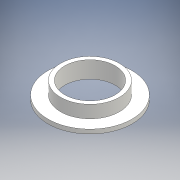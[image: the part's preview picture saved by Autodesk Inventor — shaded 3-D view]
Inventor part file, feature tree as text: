
AUTODESK INVENTOR PART (.ipt)
format: ipt  version: 2016 (Build 200138000, 138)  size: 103,936 bytes
history: native  units: mm
features: extrude x2, other x1, sketch x1
ambient origin geometry x8: Origin, YZ Plane, XZ Plane, XY Plane, X Axis, Y Axis, Z Axis, Center Point
bodies: Body1 (feature_tree)
feature tree (4):
  other  "ソリッド1"
  sketch  "スケッチ1"
  extrude  "押し出し1"  Depth=12.0mm
  extrude  "押し出し2"  Depth=14.0mm
